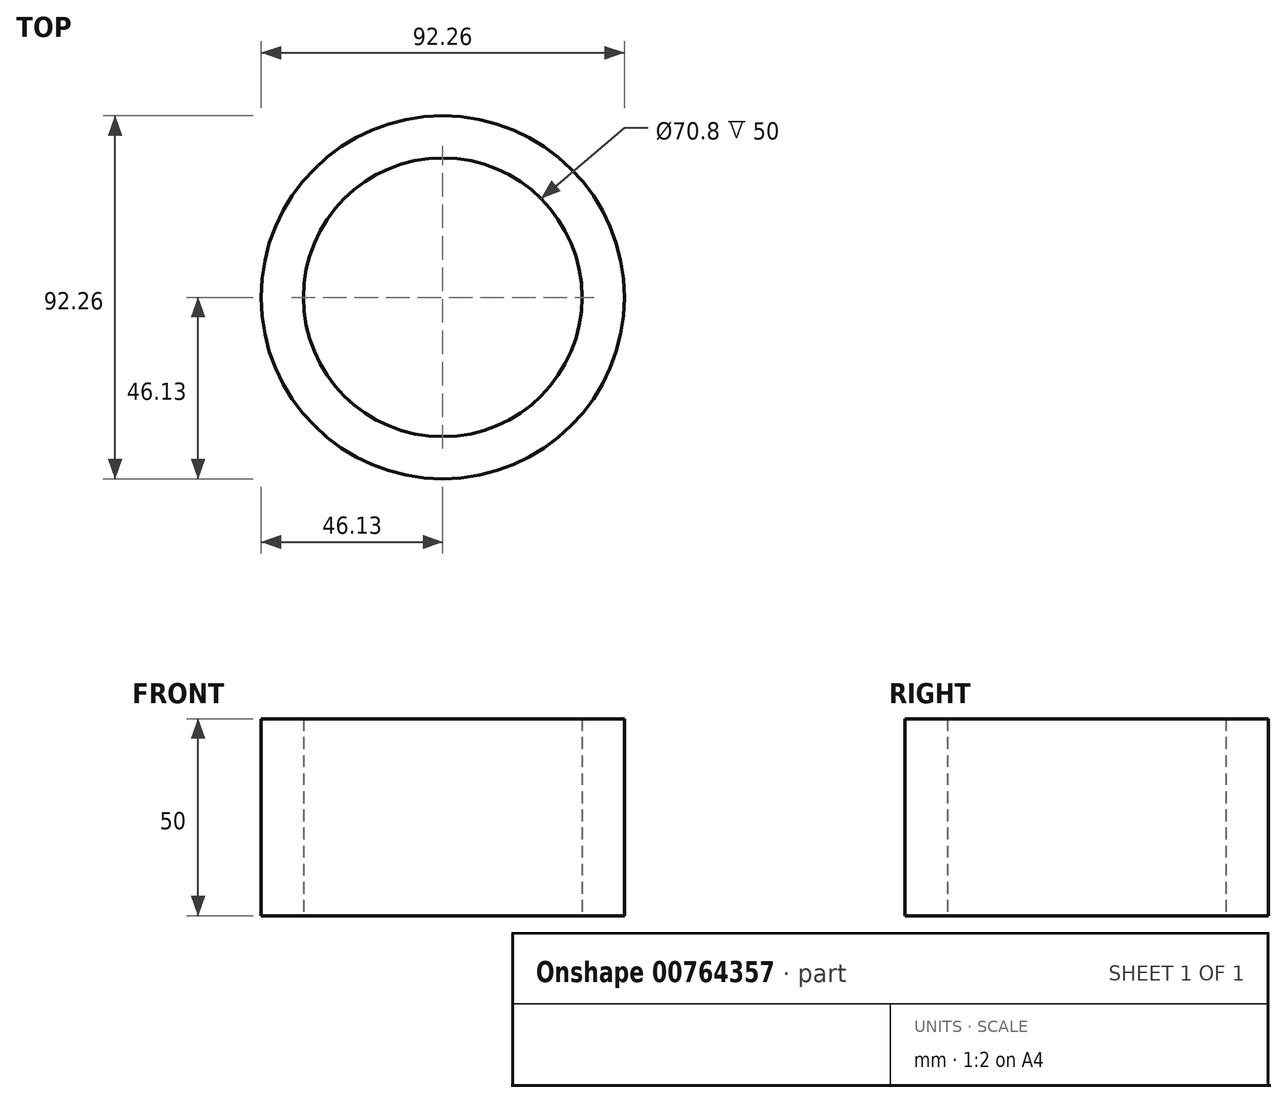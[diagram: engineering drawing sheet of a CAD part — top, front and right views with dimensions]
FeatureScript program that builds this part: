
annotation { "Feature Type Name" : "Feature", "Feature Type Description" : "" }
export const myFeature = defineFeature(function(context is Context, id is Id, definition is map)
    precondition{}
    {
        {
            var Q0;
            Q0=qCreatedBy(makeId("Top.planeOp"),FACE);
            var sketch = newSketch(context, id + "F0", { "sketchPlane" : qUnion([Q0])});
            skCircle(sketch, "E0", {"center": v(0, 0) * mm, "radius": 46.13 * mm});
            skCircle(sketch, "E1", {"center": v(0, 0) * mm, "radius": 35.4 * mm});
            skSolve(sketch);
        }
        {
            var Q0;
            Q0=makeQuery(id+"F0.imprint","IMPRINT",FACE,{"disambiguationData":[TD([[makeQuery(id+"F0.imprint","IMPRINT",EDGE,{"derivedFrom":sQuery(id+"F0.wireOp",EDGE,"E0")}),1.0]])]});
            extrude(context, id + "F1", {"entities" : qUnion([Q0]), "endBound" : BoundingType.SYMMETRIC, "depth" : 50 * mm, "offsetDistance" : 25 * mm});
        }
    });
